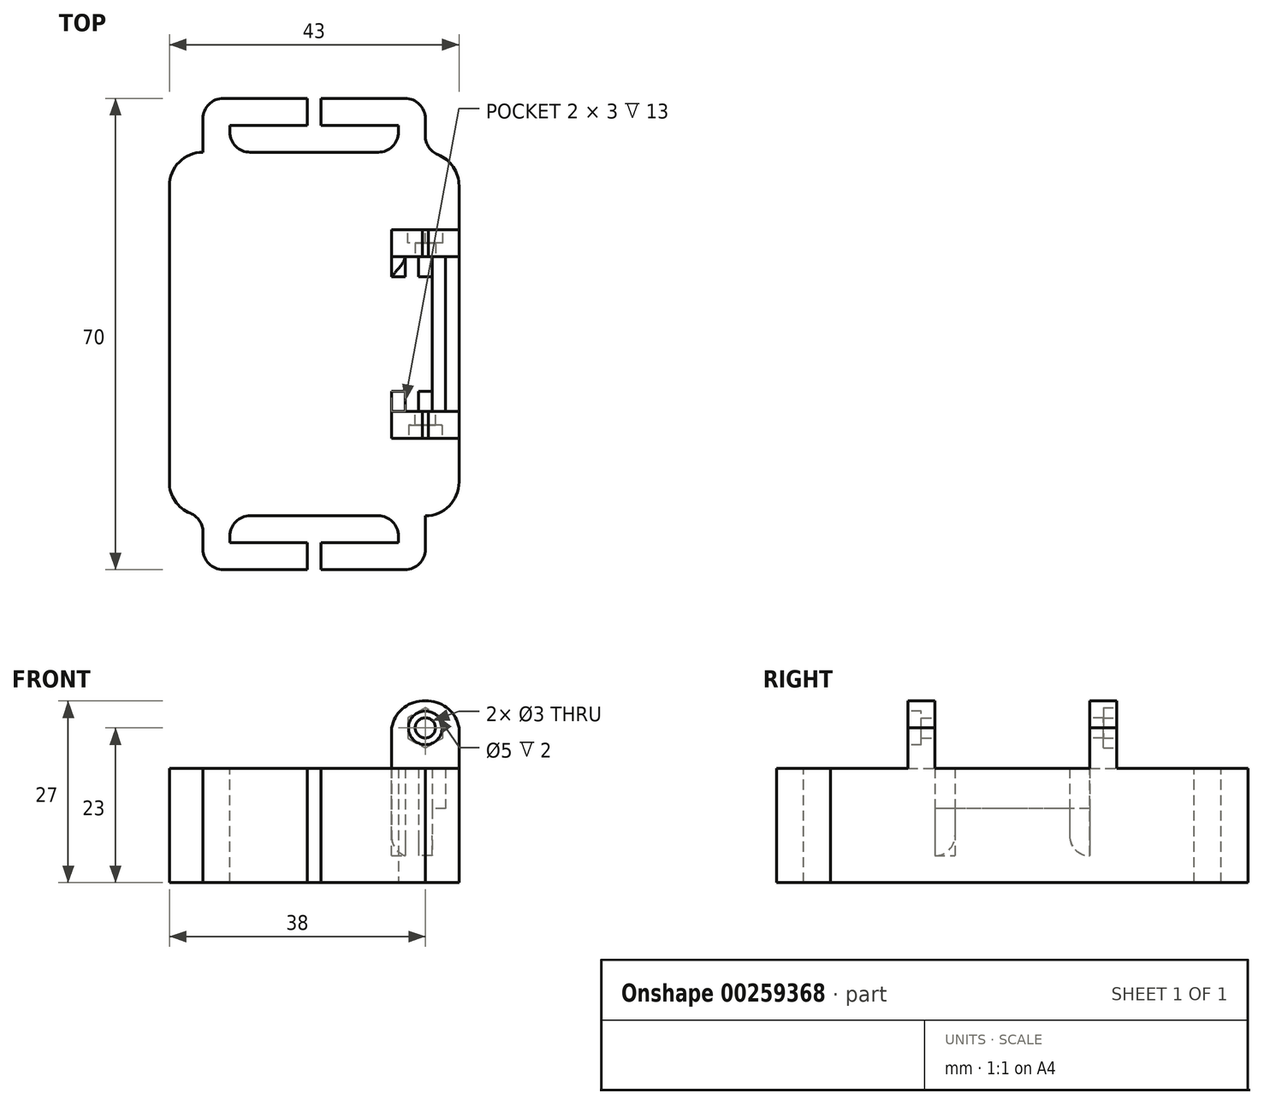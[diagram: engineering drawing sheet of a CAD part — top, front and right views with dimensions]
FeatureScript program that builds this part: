
annotation { "Feature Type Name" : "Feature", "Feature Type Description" : "" }
export const myFeature = defineFeature(function(context is Context, id is Id, definition is map)
    precondition{}
    {
        {
            var Q0;
            Q0=qCreatedBy(makeId("Front.planeOp"),FACE);
            cPlane(context, id + "F0", {"entities" : qUnion([Q0]), "cplaneType" : CPlaneType.OFFSET, "offset" : 11.5 * mm, "width" : 150 * mm, "height" : 150 * mm});
        }
        {
            var Q0;
            Q0=qCreatedBy(id+"F0.planeOp",FACE);
            var sketch = newSketch(context, id + "F1", { "sketchPlane" : qUnion([Q0])});
            skLineSegment(sketch, "E0.bottom", {"start": v(0, 0) * mm, "end": v(-10, 0) * mm});
            skLineSegment(sketch, "E0.top", {"start": v(-4.53, 23) * mm, "end": v(-5.47, 23) * mm});
            skLineSegment(sketch, "E0.left", {"start": v(0, 0) * mm, "end": v(0, 19) * mm});
            skLineSegment(sketch, "E0.right", {"start": v(-10, 0) * mm, "end": v(-10, 19) * mm});
            skCircle(sketch, "E1", {"center": v(-5, 19) * mm, "radius": 1.5 * mm});
            skLineSegment(sketch, "E2", {"start": v(-5, 23) * mm, "end": v(-5, 19) * mm, "construction": true});
            skArc(sketch, "E3", {"start": v(0, 19) * mm, "mid": v(-1.74, 21.95) * mm, "end": v(-5, 23) * mm});
            skArc(sketch, "E4", {"start": v(-5, 23) * mm, "mid": v(-8.26, 21.95) * mm, "end": v(-10, 19) * mm});
            skSolve(sketch);
        }
        {
            var Q0;
            Q0=makeQuery(id+"F1.imprint","IMPRINT",FACE,{"disambiguationData":[TD([[makeQuery(id+"F1.imprint","IMPRINT",EDGE,{"derivedFrom":sQuery(id+"F1.wireOp",EDGE,"E0.bottom")}),-1.0]])]});
            extrude(context, id + "F2", {"entities" : qUnion([Q0]), "depth" : 4 * mm});
        }
        {
            var Q0;
            Q0=makeQuery(id+"F2.opExtrude","SWEPT_BODY",BODY,{"disambiguationData":[OSD([sQuery(id+"F1.wireOp",EDGE,"E0.bottom"),sQuery(id+"F1.wireOp",EDGE,"E0.top"),sQuery(id+"F1.wireOp",EDGE,"E0.left"),sQuery(id+"F1.wireOp",EDGE,"E0.right"),sQuery(id+"F1.wireOp",EDGE,"E1"),sQuery(id+"F1.wireOp",EDGE,"E3"),sQuery(id+"F1.wireOp",EDGE,"E4")])]});
            var Q1;
            Q1=qCreatedBy(makeId("Front.planeOp"),FACE);
            mirror(context, id + "F3", {"entities" : qUnion([Q0]), "mirrorPlane" : qUnion([Q1])});
        }
        {
            var Q0;
            Q0=qCreatedBy(makeId("Top.planeOp"),FACE);
            var sketch = newSketch(context, id + "F4", { "sketchPlane" : qUnion([Q0])});
            skLineSegment(sketch, "E5.bottom", {"start": v(0, -27) * mm, "end": v(-43, -27) * mm});
            skLineSegment(sketch, "E5.top", {"start": v(0, 27) * mm, "end": v(-43, 27) * mm});
            skLineSegment(sketch, "E5.left", {"start": v(0, -27) * mm, "end": v(0, 27) * mm});
            skLineSegment(sketch, "E5.right", {"start": v(-43, -27) * mm, "end": v(-43, 27) * mm});
            skSolve(sketch);
        }
        {
            var Q0;
            Q0=makeQuery(id+"F4.imprint","IMPRINT",FACE,{"disambiguationData":[TD([[makeQuery(id+"F4.imprint","IMPRINT",EDGE,{"derivedFrom":sQuery(id+"F4.wireOp",EDGE,"E5.bottom")}),-1.0]])]});
            extrude(context, id + "F5", {"entities" : qUnion([Q0]), "oppositeDirection" : true, "depth" : 4 * mm});
        }
        {
            var Q0;
            Q0=makeQuery(id+"F2.opExtrude","CAP_EDGE",EDGE,{"disambiguationData":[OSD([sQuery(id+"F1.wireOp",EDGE,"E0.bottom")])],"isStart":false});
            var Q1;
            Q1=makeQuery(id+"F3.opPattern","COPY",EDGE,{"derivedFrom":makeQuery(id+"F2.opExtrude","CAP_EDGE",EDGE,{"disambiguationData":[OSD([sQuery(id+"F1.wireOp",EDGE,"E0.bottom")])],"isStart":false}),"instanceName":"1"});
            var Q2;
            Q2=makeQuery(id+"F3.opPattern","COPY",EDGE,{"derivedFrom":makeQuery(id+"F2.opExtrude","SWEPT_EDGE",EDGE,{"disambiguationData":[OSD([sQuery(id+"F1.wireOp",EDGE,"E0.bottom"),sQuery(id+"F1.wireOp",EDGE,"E0.right")])]}),"instanceName":"1"});
            var Q3;
            Q3=makeQuery(id+"F2.opExtrude","SWEPT_EDGE",EDGE,{"disambiguationData":[OSD([sQuery(id+"F1.wireOp",EDGE,"E0.bottom"),sQuery(id+"F1.wireOp",EDGE,"E0.right")])]});
            var Q4;
            Q4=makeQuery(id+"F5.opExtrude","SWEPT_EDGE",EDGE,{"disambiguationData":[OSD([sQuery(id+"F4.wireOp",EDGE,"E5.top"),sQuery(id+"F4.wireOp",EDGE,"E5.right")])]});
            var Q5;
            Q5=makeQuery(id+"F5.opExtrude","SWEPT_EDGE",EDGE,{"disambiguationData":[OSD([sQuery(id+"F4.wireOp",EDGE,"E5.bottom"),sQuery(id+"F4.wireOp",EDGE,"E5.right")])]});
            var Q6;
            Q6=makeQuery(id+"F5.opExtrude","SWEPT_EDGE",EDGE,{"disambiguationData":[OSD([sQuery(id+"F4.wireOp",EDGE,"E5.bottom"),sQuery(id+"F4.wireOp",EDGE,"E5.left")])]});
            var Q7;
            Q7=makeQuery(id+"F5.opExtrude","SWEPT_EDGE",EDGE,{"disambiguationData":[OSD([sQuery(id+"F4.wireOp",EDGE,"E5.top"),sQuery(id+"F4.wireOp",EDGE,"E5.left")])]});
            fillet(context, id + "F6", {"entities" : qUnion([Q0, Q1, Q2, Q3, Q4, Q5, Q6, Q7]), "radius" : 5 * mm, "tangentPropagation" : true, "allowEdgeOverflow" : false});
        }
        {
            var Q0;
            Q0=makeQuery(id+"F5.opExtrude","SWEPT_FACE",FACE,{"disambiguationData":[OSD([sQuery(id+"F4.wireOp",EDGE,"E5.top")])]});
            var sketch = newSketch(context, id + "F7", { "sketchPlane" : qUnion([Q0])});
            skLineSegment(sketch, "E6.bottom", {"start": v(38, 0) * mm, "end": v(34, 0) * mm});
            skLineSegment(sketch, "E6.top", {"start": v(38, -4) * mm, "end": v(34, -4) * mm});
            skLineSegment(sketch, "E6.left", {"start": v(38, 0) * mm, "end": v(38, -4) * mm});
            skLineSegment(sketch, "E6.right", {"start": v(34, 0) * mm, "end": v(34, -4) * mm});
            skLineSegment(sketch, "E7.bottom", {"start": v(5, -4) * mm, "end": v(9, -4) * mm});
            skLineSegment(sketch, "E7.top", {"start": v(5, 0) * mm, "end": v(9, 0) * mm});
            skLineSegment(sketch, "E7.left", {"start": v(5, -4) * mm, "end": v(5, 0) * mm});
            skLineSegment(sketch, "E7.right", {"start": v(9, -4) * mm, "end": v(9, 0) * mm});
            skSolve(sketch);
        }
        {
            var Q0;
            Q0=makeQuery(id+"F7.imprint","IMPRINT",FACE,{"disambiguationData":[TD([[makeQuery(id+"F7.imprint","IMPRINT",EDGE,{"derivedFrom":sQuery(id+"F7.wireOp",EDGE,"E6.bottom")}),-1.0]])]});
            var Q1;
            Q1=makeQuery(id+"F7.imprint","IMPRINT",FACE,{"disambiguationData":[TD([[makeQuery(id+"F7.imprint","IMPRINT",EDGE,{"derivedFrom":sQuery(id+"F7.wireOp",EDGE,"E7.bottom")}),1.0]])]});
            extrude(context, id + "F8", {"entities" : qUnion([Q0, Q1]), "operationType" : NewBodyOperationType.ADD, "depth" : 8 * mm, "hasSecondDirection" : true, "secondDirectionOppositeDirection" : true, "secondDirectionDepth" : 62 * mm});
        }
        {
            var Q0;
            {var subQ4=sQuery(id+"F4.wireOp",EDGE,"E5.bottom");var subQ5=sQuery(id+"F7.wireOp",EDGE,"E6.right");Q0=makeQuery(id+"F8.boolean.opBoolean","SPLIT",FACE,{"disambiguationData":[TD([makeQuery(id+"F5.opExtrude","SWEPT_FACE",FACE,{"disambiguationData":[OSD([subQ4])]})])],"derivedFrom":makeQuery(id+"F8.opExtrude","SWEPT_FACE",FACE,{"disambiguationData":[OSD([subQ5])]})});}
            var sketch = newSketch(context, id + "F9", { "sketchPlane" : qUnion([Q0])});
            skLineSegment(sketch, "E8.bottom", {"start": v(-35, -4) * mm, "end": v(-31, -4) * mm});
            skLineSegment(sketch, "E8.top", {"start": v(-35, 0) * mm, "end": v(-31, 0) * mm});
            skLineSegment(sketch, "E8.left", {"start": v(-35, -4) * mm, "end": v(-35, 0) * mm});
            skLineSegment(sketch, "E8.right", {"start": v(-31, -4) * mm, "end": v(-31, 0) * mm});
            skLineSegment(sketch, "E9.bottom", {"start": v(35, 0) * mm, "end": v(31, 0) * mm});
            skLineSegment(sketch, "E9.top", {"start": v(35, -4) * mm, "end": v(31, -4) * mm});
            skLineSegment(sketch, "E9.left", {"start": v(35, 0) * mm, "end": v(35, -4) * mm});
            skLineSegment(sketch, "E9.right", {"start": v(31, 0) * mm, "end": v(31, -4) * mm});
            skSolve(sketch);
        }
        {
            var Q0;
            Q0=makeQuery(id+"F9.imprint","IMPRINT",FACE,{"disambiguationData":[TD([[makeQuery(id+"F9.imprint","IMPRINT",EDGE,{"derivedFrom":sQuery(id+"F9.wireOp",EDGE,"E8.bottom")}),-1.0]])]});
            var Q1;
            Q1=makeQuery(id+"F9.imprint","IMPRINT",FACE,{"disambiguationData":[TD([[makeQuery(id+"F9.imprint","IMPRINT",EDGE,{"derivedFrom":sQuery(id+"F9.wireOp",EDGE,"E9.bottom")}),1.0]])]});
            extrude(context, id + "F10", {"entities" : qUnion([Q0, Q1]), "operationType" : NewBodyOperationType.ADD, "depth" : 25 * mm});
        }
        {
            var Q0;
            Q0=makeQuery(id+"F10.boolean.opBoolean","MERGE",FACE,{"derivedFrom":[makeQuery(id+"F8.boolean.opBoolean","MERGE",FACE,{"derivedFrom":[makeQuery(id+"F5.opExtrude","CAP_FACE",FACE,{"disambiguationData":[OSD([sQuery(id+"F4.wireOp",EDGE,"E5.bottom"),sQuery(id+"F4.wireOp",EDGE,"E5.top"),sQuery(id+"F4.wireOp",EDGE,"E5.left"),sQuery(id+"F4.wireOp",EDGE,"E5.right")])],"isStart":true}),makeQuery(id+"F8.opExtrude","SWEPT_FACE",FACE,{"disambiguationData":[OSD([sQuery(id+"F7.wireOp",EDGE,"E6.bottom")])]}),makeQuery(id+"F8.opExtrude","SWEPT_FACE",FACE,{"disambiguationData":[OSD([sQuery(id+"F7.wireOp",EDGE,"E7.top")])]})]}),makeQuery(id+"F10.opExtrude","SWEPT_FACE",FACE,{"disambiguationData":[OSD([sQuery(id+"F9.wireOp",EDGE,"E8.top")])]}),makeQuery(id+"F10.opExtrude","SWEPT_FACE",FACE,{"disambiguationData":[OSD([sQuery(id+"F9.wireOp",EDGE,"E9.bottom")])]})]});
            var sketch = newSketch(context, id + "F11", { "sketchPlane" : qUnion([Q0])});
            skLineSegment(sketch, "E10.bottom", {"start": v(-20.5, -35) * mm, "end": v(-22.5, -35) * mm});
            skLineSegment(sketch, "E10.top", {"start": v(-20.5, -31) * mm, "end": v(-22.5, -31) * mm});
            skLineSegment(sketch, "E10.left", {"start": v(-20.5, -35) * mm, "end": v(-20.5, -31) * mm});
            skLineSegment(sketch, "E10.right", {"start": v(-22.5, -35) * mm, "end": v(-22.5, -31) * mm});
            skLineSegment(sketch, "E11.bottom", {"start": v(-20.5, 35) * mm, "end": v(-22.5, 35) * mm});
            skLineSegment(sketch, "E11.top", {"start": v(-20.5, 31) * mm, "end": v(-22.5, 31) * mm});
            skLineSegment(sketch, "E11.left", {"start": v(-20.5, 35) * mm, "end": v(-20.5, 31) * mm});
            skLineSegment(sketch, "E11.right", {"start": v(-22.5, 35) * mm, "end": v(-22.5, 31) * mm});
            skLineSegment(sketch, "E12.bottom", {"start": v(0, 11.5) * mm, "end": v(-2, 11.5) * mm});
            skLineSegment(sketch, "E12.top", {"start": v(0, -3.5) * mm, "end": v(-2, -3.5) * mm});
            skLineSegment(sketch, "E12.left", {"start": v(0, 11.5) * mm, "end": v(0, -3.5) * mm});
            skLineSegment(sketch, "E12.right", {"start": v(-2, 11.5) * mm, "end": v(-2, -3.5) * mm});
            skLineSegment(sketch, "E13.bottom", {"start": v(0, -11.5) * mm, "end": v(-2, -11.5) * mm});
            skLineSegment(sketch, "E13.left", {"start": v(0, -11.5) * mm, "end": v(0, -3.5) * mm});
            skLineSegment(sketch, "E13.right", {"start": v(-2, -11.5) * mm, "end": v(-2, -3.5) * mm});
            skLineSegment(sketch, "E14.bottom", {"start": v(-15, -11.5) * mm, "end": v(-13, -11.5) * mm});
            skLineSegment(sketch, "E15.bottom", {"start": v(-10, -11.5) * mm, "end": v(-13, -11.5) * mm});
            skPoint(sketch, "E16", {"position": v(-10, 11.5) * mm});
            skLineSegment(sketch, "E17.bottom", {"start": v(-10, 11.5) * mm, "end": v(-8, 11.5) * mm});
            skLineSegment(sketch, "E17.top", {"start": v(-10, 8.5) * mm, "end": v(-8, 8.5) * mm});
            skLineSegment(sketch, "E17.left", {"start": v(-10, 11.5) * mm, "end": v(-10, 8.5) * mm});
            skLineSegment(sketch, "E17.right", {"start": v(-8, 11.5) * mm, "end": v(-8, 8.5) * mm});
            skPoint(sketch, "E18.oppositeSnap0", {"position": v(-9, 8.5) * mm});
            skLineSegment(sketch, "E18.bottom", {"start": v(-6, 11.5) * mm, "end": v(-4, 11.5) * mm});
            skLineSegment(sketch, "E18.top", {"start": v(-6, 8.5) * mm, "end": v(-4, 8.5) * mm});
            skLineSegment(sketch, "E18.left", {"start": v(-6, 11.5) * mm, "end": v(-6, 8.5) * mm});
            skLineSegment(sketch, "E18.right", {"start": v(-4, 11.5) * mm, "end": v(-4, 8.5) * mm});
            skLineSegment(sketch, "E19", {"start": v(-6, 10) * mm, "end": v(-8, 10) * mm});
            skLineSegment(sketch, "E20.bottom", {"start": v(-10, -11.5) * mm, "end": v(-8, -11.5) * mm});
            skLineSegment(sketch, "E20.top", {"start": v(-10, -8.5) * mm, "end": v(-8, -8.5) * mm});
            skLineSegment(sketch, "E20.left", {"start": v(-10, -11.5) * mm, "end": v(-10, -8.5) * mm});
            skLineSegment(sketch, "E20.right", {"start": v(-8, -11.5) * mm, "end": v(-8, -8.5) * mm});
            skLineSegment(sketch, "E21.bottom", {"start": v(-6, -11.5) * mm, "end": v(-4, -11.5) * mm});
            skLineSegment(sketch, "E21.top", {"start": v(-6, -8.5) * mm, "end": v(-4, -8.5) * mm});
            skLineSegment(sketch, "E21.left", {"start": v(-6, -11.5) * mm, "end": v(-6, -8.5) * mm});
            skLineSegment(sketch, "E21.right", {"start": v(-4, -11.5) * mm, "end": v(-4, -8.5) * mm});
            skLineSegment(sketch, "E22", {"start": v(-6, -10) * mm, "end": v(-8, -10) * mm});
            skLineSegment(sketch, "E23.bottom", {"start": v(-2, 11.5) * mm, "end": v(-4, 11.5) * mm});
            skLineSegment(sketch, "E23.top", {"start": v(-2, -11.5) * mm, "end": v(-4, -11.5) * mm});
            skLineSegment(sketch, "E23.left", {"start": v(-2, 11.5) * mm, "end": v(-2, -11.5) * mm});
            skLineSegment(sketch, "E23.right", {"start": v(-4, 11.5) * mm, "end": v(-4, -11.5) * mm});
            skSolve(sketch);
        }
        {
            var Q0;
            Q0=makeQuery(id+"F11.imprint","IMPRINT",FACE,{"disambiguationData":[TD([[makeQuery(id+"F11.imprint","IMPRINT",EDGE,{"derivedFrom":sQuery(id+"F11.wireOp",EDGE,"E10.bottom")}),-1.0]])]});
            var Q1;
            Q1=makeQuery(id+"F11.imprint","IMPRINT",FACE,{"disambiguationData":[TD([[makeQuery(id+"F11.imprint","IMPRINT",EDGE,{"derivedFrom":sQuery(id+"F11.wireOp",EDGE,"E11.bottom")}),1.0]])]});
            extrude(context, id + "F12", {"entities" : qUnion([Q0, Q1]), "operationType" : NewBodyOperationType.REMOVE, "oppositeDirection" : true, "depth" : 5 * mm});
        }
        {
            var Q0;
            Q0=makeQuery(id+"F11.imprint","IMPRINT",FACE,{"disambiguationData":[TD([[makeQuery(id+"F11.imprint","IMPRINT",EDGE,{"derivedFrom":sQuery(id+"F11.wireOp",EDGE,"E12.bottom")}),1.0]])]});
            var Q1;
            Q1=makeQuery(id+"F11.imprint","IMPRINT",FACE,{"disambiguationData":[TD([[makeQuery(id+"F11.imprint","IMPRINT",EDGE,{"derivedFrom":sQuery(id+"F11.wireOp",EDGE,"E13.bottom")}),-1.0]])]});
            var Q2;
            {var subQ1=sQuery(id+"F11.wireOp",EDGE,"E21.bottom");Q2=makeQuery(id+"F11.imprint","IMPRINT",FACE,{"disambiguationData":[TD([[makeQuery(id+"F11.imprint","IMPRINT",EDGE,{"derivedFrom":subQ1}),-1.0]])]});}
            var Q3;
            {var subQ3=sQuery(id+"F11.wireOp",EDGE,"E22");Q3=makeQuery(id+"F11.imprint","IMPRINT",FACE,{"disambiguationData":[TD([[makeQuery(id+"F11.imprint","IMPRINT",EDGE,{"derivedFrom":subQ3}),1.0]])]});}
            var Q4;
            {var subQ1=sQuery(id+"F11.wireOp",EDGE,"E20.bottom");Q4=makeQuery(id+"F11.imprint","IMPRINT",FACE,{"disambiguationData":[TD([[makeQuery(id+"F11.imprint","IMPRINT",EDGE,{"derivedFrom":subQ1}),-1.0]])]});}
            var Q5;
            {var subQ1=sQuery(id+"F11.wireOp",EDGE,"E17.bottom");Q5=makeQuery(id+"F11.imprint","IMPRINT",FACE,{"disambiguationData":[TD([[makeQuery(id+"F11.imprint","IMPRINT",EDGE,{"derivedFrom":subQ1}),1.0]])]});}
            var Q6;
            {var subQ3=sQuery(id+"F11.wireOp",EDGE,"E19");Q6=makeQuery(id+"F11.imprint","IMPRINT",FACE,{"disambiguationData":[TD([[makeQuery(id+"F11.imprint","IMPRINT",EDGE,{"derivedFrom":subQ3}),-1.0]])]});}
            var Q7;
            {var subQ3=sQuery(id+"F11.wireOp",EDGE,"E18.bottom");Q7=makeQuery(id+"F11.imprint","IMPRINT",FACE,{"disambiguationData":[TD([[makeQuery(id+"F11.imprint","IMPRINT",EDGE,{"derivedFrom":subQ3}),1.0]])]});}
            extrude(context, id + "F13", {"entities" : qUnion([Q0, Q1, Q2, Q3, Q4, Q5, Q6, Q7]), "operationType" : NewBodyOperationType.ADD, "depth" : 13 * mm});
        }
        {
            var Q0;
            {var subQ5=sQuery(id+"F11.wireOp",EDGE,"E23.bottom");Q0=makeQuery(id+"F11.imprint","IMPRINT",FACE,{"disambiguationData":[TD([[makeQuery(id+"F11.imprint","IMPRINT",EDGE,{"derivedFrom":subQ5}),1.0]])]});}
            extrude(context, id + "F14", {"entities" : qUnion([Q0]), "operationType" : NewBodyOperationType.ADD, "depth" : 7 * mm});
        }
        {
            var Q0;
            Q0=makeQuery(id+"F13.opExtrude","CAP_EDGE",EDGE,{"disambiguationData":[OSD([sQuery(id+"F11.wireOp",EDGE,"E20.left")])],"isStart":true});
            var Q1;
            Q1=makeQuery(id+"F13.opExtrude","CAP_EDGE",EDGE,{"disambiguationData":[OSD([sQuery(id+"F11.wireOp",EDGE,"E17.left")])],"isStart":true});
            var Q2;
            Q2=makeQuery(id+"F13.opExtrude","CAP_EDGE",EDGE,{"disambiguationData":[OSD([sQuery(id+"F11.wireOp",EDGE,"E20.top")])],"isStart":true});
            var Q3;
            Q3=makeQuery(id+"F13.opExtrude","CAP_EDGE",EDGE,{"disambiguationData":[OSD([sQuery(id+"F11.wireOp",EDGE,"E17.top")])],"isStart":true});
            var Q4;
            Q4=makeQuery(id+"F8.opExtrude","CAP_EDGE",EDGE,{"disambiguationData":[OSD([sQuery(id+"F7.wireOp",EDGE,"E7.left")])],"isStart":true});
            var Q5;
            Q5=makeQuery(id+"F8.opExtrude","CAP_EDGE",EDGE,{"disambiguationData":[OSD([sQuery(id+"F7.wireOp",EDGE,"E6.left")])],"isStart":true});
            var Q6;
            Q6=makeQuery(id+"F8.boolean.opBoolean","INTERSECT",EDGE,{"derivedFrom":[makeQuery(id+"F5.opExtrude","SWEPT_FACE",FACE,{"disambiguationData":[OSD([sQuery(id+"F4.wireOp",EDGE,"E5.bottom")])]}),makeQuery(id+"F8.opExtrude","SWEPT_FACE",FACE,{"disambiguationData":[OSD([sQuery(id+"F7.wireOp",EDGE,"E7.right")])]})]});
            var Q7;
            Q7=makeQuery(id+"F8.boolean.opBoolean","INTERSECT",EDGE,{"derivedFrom":[makeQuery(id+"F5.opExtrude","SWEPT_FACE",FACE,{"disambiguationData":[OSD([sQuery(id+"F4.wireOp",EDGE,"E5.bottom")])]}),makeQuery(id+"F8.opExtrude","SWEPT_FACE",FACE,{"disambiguationData":[OSD([sQuery(id+"F7.wireOp",EDGE,"E6.right")])]})]});
            var Q8;
            Q8=makeQuery(id+"F10.opExtrude","CAP_EDGE",EDGE,{"disambiguationData":[OSD([sQuery(id+"F9.wireOp",EDGE,"E8.right")])],"isStart":true});
            var Q9;
            Q9=makeQuery(id+"F10.opExtrude","CAP_EDGE",EDGE,{"disambiguationData":[OSD([sQuery(id+"F9.wireOp",EDGE,"E8.right")])],"isStart":false});
            var Q10;
            {var subQ0=sQuery(id+"F4.wireOp",EDGE,"E5.bottom");Q10=makeQuery(id+"F6.opFillet","BLEND_EDGE",EDGE,{"blendedFrom":[makeQuery(id+"F5.opExtrude","SWEPT_EDGE",EDGE,{"disambiguationData":[OSD([subQ0,sQuery(id+"F4.wireOp",EDGE,"E5.right")])]}),makeQuery(id+"F5.opExtrude","SWEPT_FACE",FACE,{"disambiguationData":[OSD([subQ0])]})],"blendedInto":[makeQuery(id+"F5.opExtrude","SWEPT_FACE",FACE,{"disambiguationData":[OSD([subQ0])]})]});}
            var Q11;
            {var subQ0=sQuery(id+"F4.wireOp",EDGE,"E5.bottom");Q11=makeQuery(id+"F6.opFillet","BLEND_EDGE",EDGE,{"blendedFrom":[makeQuery(id+"F5.opExtrude","SWEPT_EDGE",EDGE,{"disambiguationData":[OSD([subQ0,sQuery(id+"F4.wireOp",EDGE,"E5.left")])]}),makeQuery(id+"F5.opExtrude","SWEPT_FACE",FACE,{"disambiguationData":[OSD([subQ0])]})],"blendedInto":[makeQuery(id+"F5.opExtrude","SWEPT_FACE",FACE,{"disambiguationData":[OSD([subQ0])]})]});}
            var Q12;
            {var subQ0=sQuery(id+"F4.wireOp",EDGE,"E5.top");Q12=makeQuery(id+"F6.opFillet","BLEND_EDGE",EDGE,{"blendedFrom":[makeQuery(id+"F5.opExtrude","SWEPT_EDGE",EDGE,{"disambiguationData":[OSD([subQ0,sQuery(id+"F4.wireOp",EDGE,"E5.right")])]}),makeQuery(id+"F5.opExtrude","SWEPT_FACE",FACE,{"disambiguationData":[OSD([subQ0])]})],"blendedInto":[makeQuery(id+"F5.opExtrude","SWEPT_FACE",FACE,{"disambiguationData":[OSD([subQ0])]})]});}
            var Q13;
            Q13=makeQuery(id+"F8.opExtrude","CAP_EDGE",EDGE,{"disambiguationData":[OSD([sQuery(id+"F7.wireOp",EDGE,"E6.left")])],"isStart":false});
            var Q14;
            Q14=makeQuery(id+"F8.boolean.opBoolean","INTERSECT",EDGE,{"derivedFrom":[makeQuery(id+"F5.opExtrude","SWEPT_FACE",FACE,{"disambiguationData":[OSD([sQuery(id+"F4.wireOp",EDGE,"E5.top")])]}),makeQuery(id+"F8.opExtrude","SWEPT_FACE",FACE,{"disambiguationData":[OSD([sQuery(id+"F7.wireOp",EDGE,"E7.right")])]})]});
            var Q15;
            {var subQ0=sQuery(id+"F4.wireOp",EDGE,"E5.top");Q15=makeQuery(id+"F6.opFillet","BLEND_EDGE",EDGE,{"blendedFrom":[makeQuery(id+"F5.opExtrude","SWEPT_EDGE",EDGE,{"disambiguationData":[OSD([subQ0,sQuery(id+"F4.wireOp",EDGE,"E5.left")])]}),makeQuery(id+"F5.opExtrude","SWEPT_FACE",FACE,{"disambiguationData":[OSD([subQ0])]})],"blendedInto":[makeQuery(id+"F5.opExtrude","SWEPT_FACE",FACE,{"disambiguationData":[OSD([subQ0])]})]});}
            var Q16;
            Q16=makeQuery(id+"F8.opExtrude","CAP_EDGE",EDGE,{"disambiguationData":[OSD([sQuery(id+"F7.wireOp",EDGE,"E7.left")])],"isStart":false});
            var Q17;
            Q17=makeQuery(id+"F8.boolean.opBoolean","INTERSECT",EDGE,{"derivedFrom":[makeQuery(id+"F5.opExtrude","SWEPT_FACE",FACE,{"disambiguationData":[OSD([sQuery(id+"F4.wireOp",EDGE,"E5.top")])]}),makeQuery(id+"F8.opExtrude","SWEPT_FACE",FACE,{"disambiguationData":[OSD([sQuery(id+"F7.wireOp",EDGE,"E6.right")])]})]});
            var Q18;
            Q18=makeQuery(id+"F10.opExtrude","CAP_EDGE",EDGE,{"disambiguationData":[OSD([sQuery(id+"F9.wireOp",EDGE,"E9.right")])],"isStart":true});
            var Q19;
            Q19=makeQuery(id+"F10.opExtrude","CAP_EDGE",EDGE,{"disambiguationData":[OSD([sQuery(id+"F9.wireOp",EDGE,"E9.right")])],"isStart":false});
            var Q20;
            Q20=makeQuery(id+"F13.opExtrude","CAP_EDGE",EDGE,{"disambiguationData":[OSD([sQuery(id+"F11.wireOp",EDGE,"E18.top")])],"isStart":true});
            var Q21;
            Q21=makeQuery(id+"F13.opExtrude","CAP_EDGE",EDGE,{"disambiguationData":[OSD([sQuery(id+"F11.wireOp",EDGE,"E21.top")])],"isStart":true});
            fillet(context, id + "F15", {"entities" : qUnion([Q0, Q1, Q2, Q3, Q4, Q5, Q6, Q7, Q8, Q9, Q10, Q11, Q12, Q13, Q14, Q15, Q16, Q17, Q18, Q19, Q20, Q21]), "radius" : 3 * mm, "tangentPropagation" : true, "allowEdgeOverflow" : false});
        }
        {
            var Q0;
            Q0=makeQuery(id+"F2.opExtrude","CAP_FACE",FACE,{"disambiguationData":[OSD([sQuery(id+"F1.wireOp",EDGE,"E0.bottom"),sQuery(id+"F1.wireOp",EDGE,"E0.top"),sQuery(id+"F1.wireOp",EDGE,"E0.left"),sQuery(id+"F1.wireOp",EDGE,"E0.right"),sQuery(id+"F1.wireOp",EDGE,"E1"),sQuery(id+"F1.wireOp",EDGE,"E3"),sQuery(id+"F1.wireOp",EDGE,"E4")])],"isStart":false});
            var sketch = newSketch(context, id + "F16", { "sketchPlane" : qUnion([Q0])});
            skCircle(sketch, "E24", {"center": v(-5, 19) * mm, "radius": 2.5 * mm});
            skSolve(sketch);
        }
        {
            var Q0;
            Q0=makeQuery(id+"F16.imprint","IMPRINT",FACE,{"disambiguationData":[TD([[makeQuery(id+"F16.imprint","IMPRINT",EDGE,{"derivedFrom":sQuery(id+"F16.wireOp",EDGE,"E24")}),1.0]])]});
            extrude(context, id + "F17", {"entities" : qUnion([Q0]), "operationType" : NewBodyOperationType.REMOVE, "oppositeDirection" : true, "depth" : 2 * mm});
        }
        {
            var Q0;
            Q0=makeQuery(id+"F3.opPattern","COPY",FACE,{"derivedFrom":makeQuery(id+"F2.opExtrude","CAP_FACE",FACE,{"disambiguationData":[OSD([sQuery(id+"F1.wireOp",EDGE,"E0.bottom"),sQuery(id+"F1.wireOp",EDGE,"E0.top"),sQuery(id+"F1.wireOp",EDGE,"E0.left"),sQuery(id+"F1.wireOp",EDGE,"E0.right"),sQuery(id+"F1.wireOp",EDGE,"E1"),sQuery(id+"F1.wireOp",EDGE,"E3"),sQuery(id+"F1.wireOp",EDGE,"E4")])],"isStart":false}),"instanceName":"1"});
            var sketch = newSketch(context, id + "F18", { "sketchPlane" : qUnion([Q0])});
            skCircle(sketch, "E25.cCircle", {"center": v(5, 19) * mm, "radius": 2.6 * mm, "construction": true});
            skLineSegment(sketch, "E25.0", {"start": v(7.6, 20.5) * mm, "end": v(7.6, 17.5) * mm});
            skLineSegment(sketch, "E25.1", {"start": v(7.6, 17.5) * mm, "end": v(5, 16) * mm});
            skLineSegment(sketch, "E25.2", {"start": v(5, 16) * mm, "end": v(2.4, 17.5) * mm});
            skLineSegment(sketch, "E25.3", {"start": v(2.4, 17.5) * mm, "end": v(2.4, 20.5) * mm});
            skLineSegment(sketch, "E25.4", {"start": v(2.4, 20.5) * mm, "end": v(5, 22) * mm});
            skLineSegment(sketch, "E25.5", {"start": v(5, 22) * mm, "end": v(7.6, 20.5) * mm});
            skPoint(sketch, "E25.0.midPoint", {"position": v(7.6, 19) * mm});
            skSolve(sketch);
        }
        {
            var Q0;
            Q0=makeQuery(id+"F18.imprint","IMPRINT",FACE,{"disambiguationData":[TD([[makeQuery(id+"F18.imprint","IMPRINT",EDGE,{"derivedFrom":sQuery(id+"F18.wireOp",EDGE,"E25.0")}),-1.0]])]});
            extrude(context, id + "F19", {"entities" : qUnion([Q0]), "operationType" : NewBodyOperationType.REMOVE, "oppositeDirection" : true, "depth" : 2 * mm});
        }
    });
